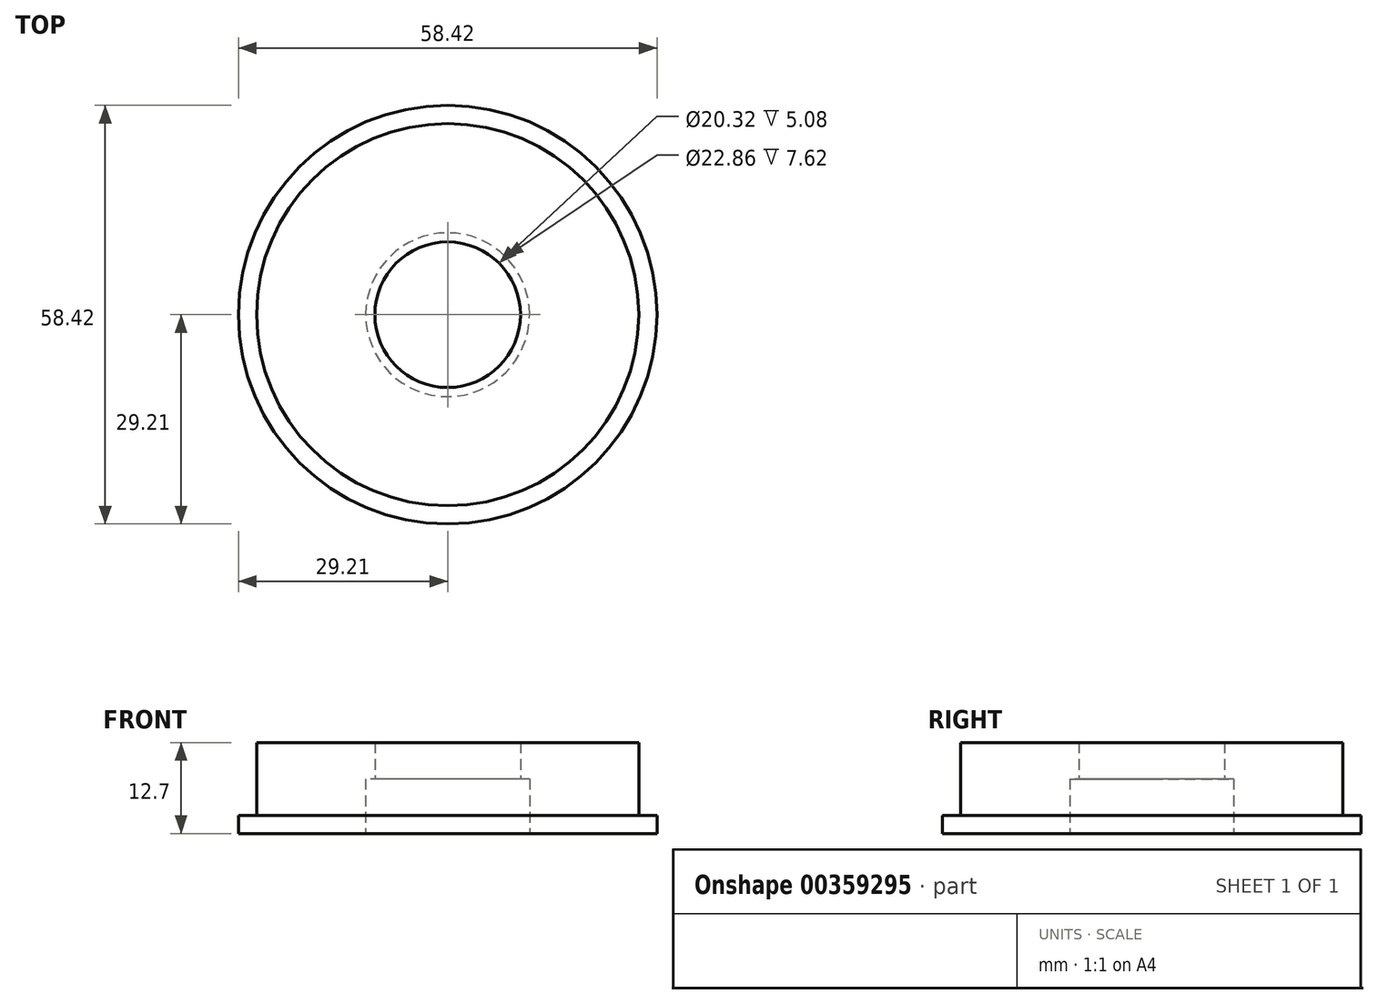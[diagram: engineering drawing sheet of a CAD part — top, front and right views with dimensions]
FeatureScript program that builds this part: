
annotation { "Feature Type Name" : "Feature", "Feature Type Description" : "" }
export const myFeature = defineFeature(function(context is Context, id is Id, definition is map)
    precondition{}
    {
        {
            var Q0;
            Q0=qCreatedBy(makeId("Top.planeOp"),FACE);
            var sketch = newSketch(context, id + "F0", { "sketchPlane" : qUnion([Q0])});
            skCircle(sketch, "E0", {"center": v(0, 0) * mm, "radius": 29.21 * mm});
            skSolve(sketch);
        }
        {
            var Q0;
            Q0=makeQuery(id+"F0.imprint","IMPRINT",FACE,{"disambiguationData":[TD([[makeQuery(id+"F0.imprint","IMPRINT",EDGE,{"derivedFrom":sQuery(id+"F0.wireOp",EDGE,"E0")}),1.0]])]});
            extrude(context, id + "F1", {"entities" : qUnion([Q0]), "depth" : 2.54 * mm});
        }
        {
            var Q0;
            Q0=qCreatedBy(makeId("Top.planeOp"),FACE);
            var sketch = newSketch(context, id + "F2", { "sketchPlane" : qUnion([Q0])});
            skCircle(sketch, "E1", {"center": v(0, 0) * mm, "radius": 26.67 * mm});
            skSolve(sketch);
        }
        {
            var Q0;
            Q0 = qSketchRegion(id + "F2", true);
            extrude(context, id + "F3", {"entities" : qUnion([Q0]), "operationType" : NewBodyOperationType.ADD, "depth" : 12.7 * mm});
        }
        {
            var Q0;
            Q0=qCreatedBy(makeId("Top.planeOp"),FACE);
            var sketch = newSketch(context, id + "F4", { "sketchPlane" : qUnion([Q0])});
            skCircle(sketch, "E2", {"center": v(0, 0) * mm, "radius": 10.16 * mm});
            skSolve(sketch);
        }
        {
            var Q0;
            Q0=makeQuery(id+"F4.imprint","IMPRINT",FACE,{"disambiguationData":[TD([[makeQuery(id+"F4.imprint","IMPRINT",EDGE,{"derivedFrom":sQuery(id+"F4.wireOp",EDGE,"E2")}),1.0]])]});
            extrude(context, id + "F5", {"entities" : qUnion([Q0]), "operationType" : NewBodyOperationType.REMOVE, "endBound" : BoundingType.THROUGH_ALL, "depth" : 25.4 * mm});
        }
        {
            var Q0;
            Q0=qCreatedBy(makeId("Top.planeOp"),FACE);
            var sketch = newSketch(context, id + "F6", { "sketchPlane" : qUnion([Q0])});
            skCircle(sketch, "E3", {"center": v(0, 0) * mm, "radius": 11.43 * mm});
            skSolve(sketch);
        }
        {
            var Q0;
            Q0 = qSketchRegion(id + "F6", true);
            extrude(context, id + "F7", {"entities" : qUnion([Q0]), "operationType" : NewBodyOperationType.REMOVE, "depth" : 7.62 * mm});
        }
    });
